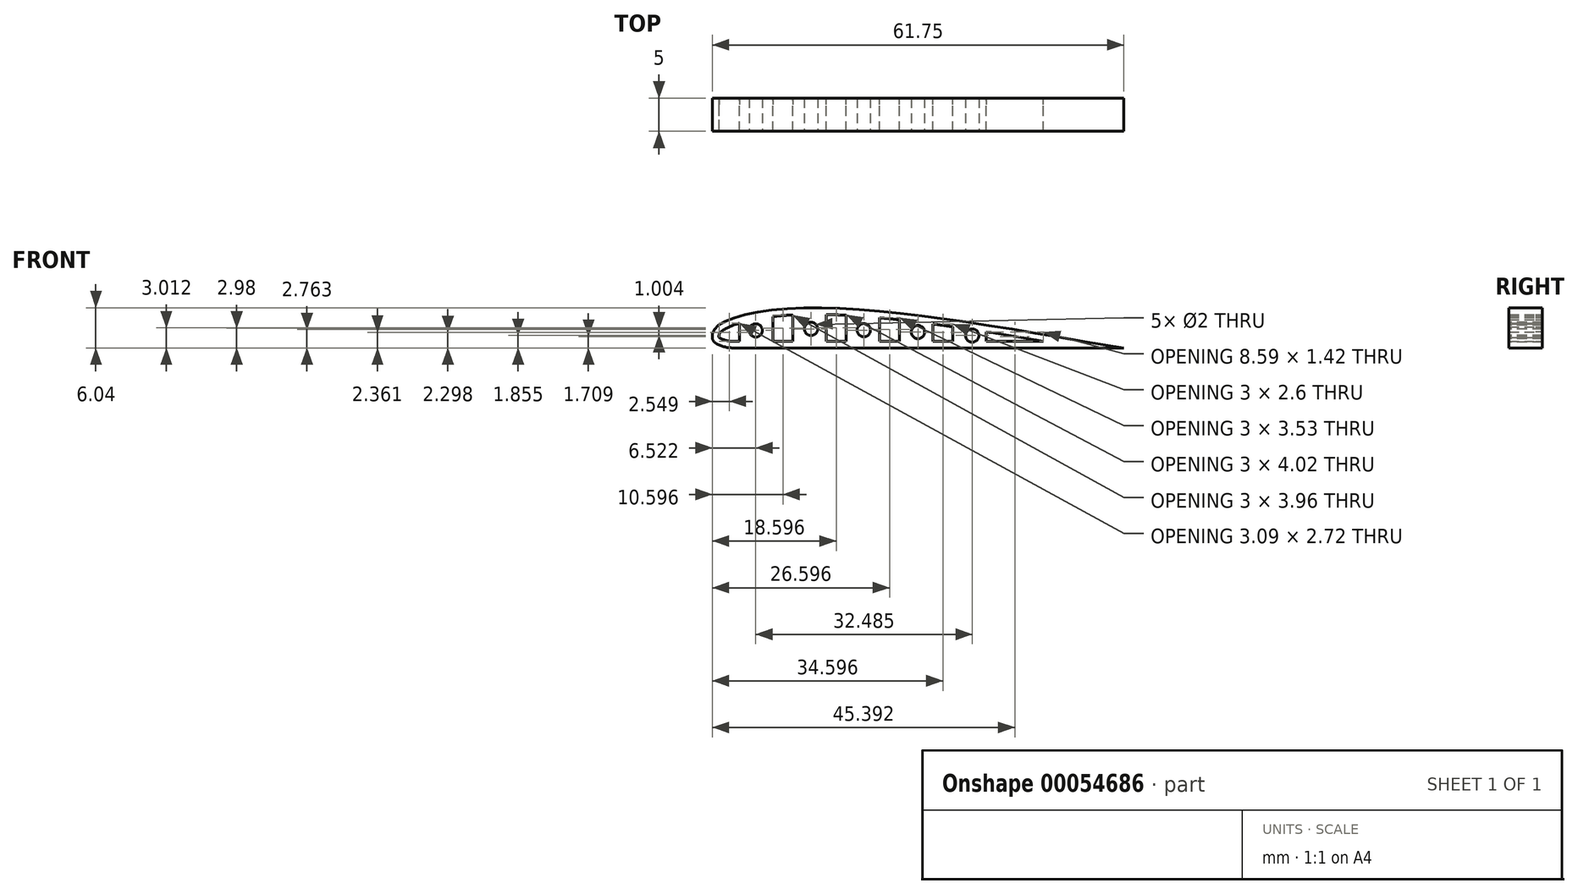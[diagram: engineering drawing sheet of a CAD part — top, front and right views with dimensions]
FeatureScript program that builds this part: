
annotation { "Feature Type Name" : "Feature", "Feature Type Description" : "" }
export const myFeature = defineFeature(function(context is Context, id is Id, definition is map)
    precondition{}
    {
        {
            var Q0;
            Q0=qCreatedBy(makeId("Front.planeOp"),FACE);
            var sketch = newSketch(context, id + "F0", { "sketchPlane" : qUnion([Q0])});
            skLineSegment(sketch, "E0.bottom", {"start": v(-37.5, 15) * mm, "end": v(37.5, 15) * mm});
            skLineSegment(sketch, "E0.top", {"start": v(-37.5, -15) * mm, "end": v(37.5, -15) * mm});
            skLineSegment(sketch, "E0.left", {"start": v(-37.5, 15) * mm, "end": v(-37.5, -15) * mm});
            skLineSegment(sketch, "E0.right", {"start": v(37.5, 15) * mm, "end": v(37.5, -15) * mm});
            skSolve(sketch);
        }
        {
            var Q0;
            Q0=makeQuery(id+"F0.imprint","IMPRINT",FACE,{"disambiguationData":[TD([[makeQuery(id+"F0.imprint","IMPRINT",EDGE,{"derivedFrom":sQuery(id+"F0.wireOp",EDGE,"E0.bottom")}),-1.0]])]});
            var sketch = newSketch(context, id + "F1", { "sketchPlane" : qUnion([Q0])});
            skLineSegment(sketch, "E1", {"start": v(33.64, -15.05) * mm, "end": v(-26.41, -15.05) * mm});
            skLineSegment(sketch, "E2", {"start": v(-26.41, -15.05) * mm, "end": v(33.64, -15.05) * mm});
            skFitSpline(sketch, "E3", {"points": [v(-26.41, -15.05) * mm, v(-27.49, -14.56) * mm, v(-28.34, -13.98) * mm], "startDerivative": vector(-2.16, 0.87) * mm, "endDerivative": vector(-1.68, 1.26) * mm});
            skFitSpline(sketch, "E4", {"points": [v(-28.34, -13.98) * mm, v(-28.07, -12.16) * mm, v(-16.6, -9.05) * mm, v(27.1, -13.98) * mm], "startDerivative": vector(-2.15, 15.6) * mm, "endDerivative": vector(83.94, -14.46) * mm});
            skLineSegment(sketch, "E5", {"start": v(27.1, -13.98) * mm, "end": v(33.64, -15.05) * mm});
            skSolve(sketch);
        }
        {
            var Q0;
            {var subQ0=sQuery(id+"F1.wireOp",EDGE,"E4");Q0=makeQuery(id+"F1.imprint","IMPRINT",FACE,{"disambiguationData":[TD([[makeQuery(id+"F1.imprint","IMPRINT",EDGE,{"derivedFrom":subQ0}),-1.0]])]});}
            extrude(context, id + "F2", {"entities" : qUnion([Q0]), "depth" : 5 * mm});
        }
        {
            var Q0;
            Q0=makeQuery(id+"F2.opExtrude","SWEPT_EDGE",EDGE,{"disambiguationData":[OSD([sQuery(id+"F0.wireOp",EDGE,"E0.top"),sQuery(id+"F1.wireOp",EDGE,"E3")])]});
            fillet(context, id + "F3", {"entities" : qUnion([Q0]), "radius" : 5 * mm, "tangentPropagation" : true, "allowEdgeOverflow" : false});
        }
        {
            var Q0;
            Q0=makeQuery(id+"F2.opExtrude","SWEPT_EDGE",EDGE,{"disambiguationData":[OSD([sQuery(id+"F1.wireOp",EDGE,"E3"),sQuery(id+"F1.wireOp",EDGE,"E4")])]});
            fillet(context, id + "F4", {"entities" : qUnion([Q0]), "radius" : 1 * mm, "tangentPropagation" : true, "allowEdgeOverflow" : false});
        }
        {
            var Q0;
            Q0=makeQuery(id+"F2.opExtrude","CAP_FACE",FACE,{"disambiguationData":[OSD([sQuery(id+"F0.wireOp",EDGE,"E0.top"),sQuery(id+"F1.wireOp",EDGE,"E3"),sQuery(id+"F1.wireOp",EDGE,"E4"),sQuery(id+"F1.wireOp",EDGE,"E5")])],"isStart":false});
            var Q1;
            Q1=makeQuery(id+"F2.opExtrude","SWEPT_BODY",BODY,{"disambiguationData":[OSD([sQuery(id+"F0.wireOp",EDGE,"E0.top"),sQuery(id+"F1.wireOp",EDGE,"E3"),sQuery(id+"F1.wireOp",EDGE,"E4"),sQuery(id+"F1.wireOp",EDGE,"E5")])]});
            shell(context, id + "F5", {"entities" : qUnion([Q0]), "parts" : qUnion([Q1]), "thickness" : 1 * mm});
        }
        {
            var Q0;
            Q0=makeQuery(id+"F5.opShell","OFFSET_FACE",FACE,{"disambiguationData":[OSD([sQuery(id+"F0.wireOp",EDGE,"E0.top"),sQuery(id+"F1.wireOp",EDGE,"E3"),sQuery(id+"F1.wireOp",EDGE,"E4"),sQuery(id+"F1.wireOp",EDGE,"E5")])]});
            extrude(context, id + "F6", {"entities" : qUnion([Q0]), "operationType" : NewBodyOperationType.REMOVE, "oppositeDirection" : true, "depth" : 25 * mm});
        }
        {
            var Q0;
            Q0=qCreatedBy(makeId("Front.planeOp"),FACE);
            var sketch = newSketch(context, id + "F7", { "sketchPlane" : qUnion([Q0])});
            skLineSegment(sketch, "E6", {"start": v(-24.3, -10.76) * mm, "end": v(-24.3, -14.53) * mm});
            skLineSegment(sketch, "E7", {"start": v(-23.3, -10.6) * mm, "end": v(-23.3, -14.66) * mm});
            skLineSegment(sketch, "E8", {"start": v(-20.3, -9.96) * mm, "end": v(-20.3, -14.5) * mm});
            skLineSegment(sketch, "E9", {"start": v(-19.3, -9.97) * mm, "end": v(-19.3, -14.33) * mm});
            skLineSegment(sketch, "E10", {"start": v(-16.3, -9.87) * mm, "end": v(-16.3, -14.17) * mm});
            skLineSegment(sketch, "E11", {"start": v(-15.3, -9.72) * mm, "end": v(-15.3, -14.31) * mm});
            skLineSegment(sketch, "E12", {"start": v(-12.3, -9.67) * mm, "end": v(-12.3, -14.26) * mm});
            skLineSegment(sketch, "E13", {"start": v(-11.3, -9.59) * mm, "end": v(-11.3, -14.23) * mm});
            skLineSegment(sketch, "E14", {"start": v(-8.3, -9.76) * mm, "end": v(-8.3, -14.25) * mm});
            skLineSegment(sketch, "E15", {"start": v(-7.3, -9.69) * mm, "end": v(-7.3, -14.44) * mm});
            skLineSegment(sketch, "E16", {"start": v(-4.3, -9.96) * mm, "end": v(-4.3, -14.17) * mm});
            skLineSegment(sketch, "E17", {"start": v(-3.3, -10.07) * mm, "end": v(-3.3, -14.54) * mm});
            skLineSegment(sketch, "E18", {"start": v(-0.3, -10.3) * mm, "end": v(-0.3, -14.48) * mm});
            skLineSegment(sketch, "E19", {"start": v(0.7, -10.28) * mm, "end": v(0.7, -14.5) * mm});
            skLineSegment(sketch, "E20", {"start": v(3.7, -10.65) * mm, "end": v(3.7, -14.38) * mm});
            skLineSegment(sketch, "E21", {"start": v(4.7, -10.58) * mm, "end": v(4.7, -14.4) * mm});
            skLineSegment(sketch, "E22", {"start": v(7.7, -11.69) * mm, "end": v(7.7, -14.38) * mm});
            skLineSegment(sketch, "E23", {"start": v(8.7, -11.67) * mm, "end": v(8.7, -14.24) * mm});
            skLineSegment(sketch, "E24", {"start": v(11.7, -14.25) * mm, "end": v(11.7, -12.35) * mm});
            skLineSegment(sketch, "E25", {"start": v(12.7, -12.46) * mm, "end": v(12.7, -14.23) * mm});
            skLineSegment(sketch, "E26", {"start": v(-24.3, -10.76) * mm, "end": v(-23.3, -10.6) * mm});
            skLineSegment(sketch, "E27", {"start": v(-24.3, -14.53) * mm, "end": v(-23.3, -14.66) * mm});
            skLineSegment(sketch, "E28", {"start": v(-19.3, -14.33) * mm, "end": v(-20.3, -14.5) * mm});
            skLineSegment(sketch, "E29", {"start": v(-20.31, -10) * mm, "end": v(-19.3, -9.97) * mm});
            skLineSegment(sketch, "E30", {"start": v(-16.3, -9.87) * mm, "end": v(-15.3, -9.72) * mm});
            skLineSegment(sketch, "E31", {"start": v(-16.3, -14.17) * mm, "end": v(-15.3, -14.31) * mm});
            skLineSegment(sketch, "E32", {"start": v(-12.3, -9.67) * mm, "end": v(-11.3, -9.59) * mm});
            skLineSegment(sketch, "E33", {"start": v(-12.16, -14.4) * mm, "end": v(-11.3, -14.23) * mm});
            skLineSegment(sketch, "E34", {"start": v(-12.3, -14.26) * mm, "end": v(-11.3, -14.23) * mm});
            skLineSegment(sketch, "E35", {"start": v(-8.3, -9.76) * mm, "end": v(-7.3, -9.69) * mm});
            skLineSegment(sketch, "E36", {"start": v(-8.3, -14.25) * mm, "end": v(-7.3, -14.44) * mm});
            skLineSegment(sketch, "E37", {"start": v(-4.3, -14.17) * mm, "end": v(-3.3, -14.54) * mm});
            skLineSegment(sketch, "E38", {"start": v(-4.3, -9.96) * mm, "end": v(-3.3, -10.07) * mm});
            skLineSegment(sketch, "E39", {"start": v(-0.3, -10.3) * mm, "end": v(0.7, -10.28) * mm});
            skLineSegment(sketch, "E40", {"start": v(3.7, -10.65) * mm, "end": v(4.7, -10.58) * mm});
            skLineSegment(sketch, "E41", {"start": v(-0.3, -14.48) * mm, "end": v(0.7, -14.5) * mm});
            skLineSegment(sketch, "E42", {"start": v(3.7, -14.38) * mm, "end": v(4.7, -14.4) * mm});
            skLineSegment(sketch, "E43", {"start": v(8.7, -14.24) * mm, "end": v(7.7, -14.38) * mm});
            skLineSegment(sketch, "E44", {"start": v(11.7, -14.25) * mm, "end": v(12.7, -14.23) * mm});
            skLineSegment(sketch, "E45", {"start": v(12.7, -12.46) * mm, "end": v(11.7, -12.35) * mm});
            skLineSegment(sketch, "E46", {"start": v(8.7, -11.67) * mm, "end": v(7.7, -11.69) * mm});
            skLineSegment(sketch, "E47", {"start": v(-23.3, -10.6) * mm, "end": v(-20.3, -9.96) * mm});
            skLineSegment(sketch, "E48", {"start": v(-20.3, -14.5) * mm, "end": v(-23.3, -14.66) * mm});
            skLineSegment(sketch, "E49", {"start": v(-15.3, -9.72) * mm, "end": v(-12.3, -9.67) * mm});
            skLineSegment(sketch, "E50", {"start": v(-15.3, -14.31) * mm, "end": v(-12.3, -14.26) * mm});
            skLineSegment(sketch, "E51", {"start": v(-7.3, -14.44) * mm, "end": v(-4.3, -14.17) * mm});
            skLineSegment(sketch, "E52", {"start": v(-7.3, -9.69) * mm, "end": v(-4.3, -9.96) * mm});
            skLineSegment(sketch, "E53", {"start": v(0.7, -10.28) * mm, "end": v(3.7, -10.65) * mm});
            skLineSegment(sketch, "E54", {"start": v(0.7, -14.5) * mm, "end": v(3.7, -14.38) * mm});
            skLineSegment(sketch, "E55", {"start": v(8.7, -11.67) * mm, "end": v(11.7, -12.35) * mm});
            skLineSegment(sketch, "E56", {"start": v(8.7, -14.24) * mm, "end": v(11.7, -14.25) * mm});
            skSolve(sketch);
        }
        {
            var Q0;
            Q0=makeQuery(id+"F7.imprint","IMPRINT",FACE,{"disambiguationData":[TD([[makeQuery(id+"F7.imprint","IMPRINT",EDGE,{"derivedFrom":sQuery(id+"F7.wireOp",EDGE,"E22")}),1.0]])]});
            var Q1;
            Q1=makeQuery(id+"F7.imprint","IMPRINT",FACE,{"disambiguationData":[TD([[makeQuery(id+"F7.imprint","IMPRINT",EDGE,{"derivedFrom":sQuery(id+"F7.wireOp",EDGE,"E6")}),1.0]])]});
            var Q2;
            {var subQ4=sQuery(id+"F7.wireOp",EDGE,"E9");Q2=makeQuery(id+"F7.imprint","IMPRINT",FACE,{"disambiguationData":[TD([[makeQuery(id+"F7.imprint","IMPRINT",EDGE,{"derivedFrom":subQ4}),-1.0]])]});}
            var Q3;
            Q3=makeQuery(id+"F7.imprint","IMPRINT",FACE,{"disambiguationData":[TD([[makeQuery(id+"F7.imprint","IMPRINT",EDGE,{"derivedFrom":sQuery(id+"F7.wireOp",EDGE,"E10")}),1.0]])]});
            var Q4;
            Q4=makeQuery(id+"F7.imprint","IMPRINT",FACE,{"disambiguationData":[TD([[makeQuery(id+"F7.imprint","IMPRINT",EDGE,{"derivedFrom":sQuery(id+"F7.wireOp",EDGE,"E12")}),1.0]])]});
            var Q5;
            Q5=makeQuery(id+"F7.imprint","IMPRINT",FACE,{"disambiguationData":[TD([[makeQuery(id+"F7.imprint","IMPRINT",EDGE,{"derivedFrom":sQuery(id+"F7.wireOp",EDGE,"E14")}),1.0]])]});
            var Q6;
            Q6=makeQuery(id+"F7.imprint","IMPRINT",FACE,{"disambiguationData":[TD([[makeQuery(id+"F7.imprint","IMPRINT",EDGE,{"derivedFrom":sQuery(id+"F7.wireOp",EDGE,"E16")}),1.0]])]});
            var Q7;
            Q7=makeQuery(id+"F7.imprint","IMPRINT",FACE,{"disambiguationData":[TD([[makeQuery(id+"F7.imprint","IMPRINT",EDGE,{"derivedFrom":sQuery(id+"F7.wireOp",EDGE,"E18")}),1.0]])]});
            var Q8;
            Q8=makeQuery(id+"F7.imprint","IMPRINT",FACE,{"disambiguationData":[TD([[makeQuery(id+"F7.imprint","IMPRINT",EDGE,{"derivedFrom":sQuery(id+"F7.wireOp",EDGE,"E20")}),1.0]])]});
            var Q9;
            Q9=makeQuery(id+"F7.imprint","IMPRINT",FACE,{"disambiguationData":[TD([[makeQuery(id+"F7.imprint","IMPRINT",EDGE,{"derivedFrom":sQuery(id+"F7.wireOp",EDGE,"E24")}),-1.0]])]});
            extrude(context, id + "F8", {"entities" : qUnion([Q0, Q1, Q2, Q3, Q4, Q5, Q6, Q7, Q8, Q9]), "operationType" : NewBodyOperationType.ADD, "depth" : 5 * mm});
        }
        {
            var Q0;
            Q0=makeQuery(id+"F7.imprint","IMPRINT",FACE,{"disambiguationData":[TD([[makeQuery(id+"F7.imprint","IMPRINT",EDGE,{"derivedFrom":sQuery(id+"F7.wireOp",EDGE,"E11")}),1.0]])]});
            var Q1;
            Q1=makeQuery(id+"F7.imprint","IMPRINT",FACE,{"disambiguationData":[TD([[makeQuery(id+"F7.imprint","IMPRINT",EDGE,{"derivedFrom":sQuery(id+"F7.wireOp",EDGE,"E15")}),1.0]])]});
            var Q2;
            Q2=makeQuery(id+"F7.imprint","IMPRINT",FACE,{"disambiguationData":[TD([[makeQuery(id+"F7.imprint","IMPRINT",EDGE,{"derivedFrom":sQuery(id+"F7.wireOp",EDGE,"E23")}),1.0]])]});
            var Q3;
            Q3=makeQuery(id+"F7.imprint","IMPRINT",FACE,{"disambiguationData":[TD([[makeQuery(id+"F7.imprint","IMPRINT",EDGE,{"derivedFrom":sQuery(id+"F7.wireOp",EDGE,"E7")}),1.0]])]});
            var Q4;
            Q4=makeQuery(id+"F7.imprint","IMPRINT",FACE,{"disambiguationData":[TD([[makeQuery(id+"F7.imprint","IMPRINT",EDGE,{"derivedFrom":sQuery(id+"F7.wireOp",EDGE,"E19")}),1.0]])]});
            extrude(context, id + "F9", {"entities" : qUnion([Q0, Q1, Q2, Q3, Q4]), "operationType" : NewBodyOperationType.ADD, "depth" : 5 * mm});
        }
        {
            var Q0;
            {var subQ0=sQuery(id+"F7.wireOp",EDGE,"E24");var subQ1=sQuery(id+"F7.wireOp",EDGE,"E23");var subQ2=sQuery(id+"F7.wireOp",EDGE,"E20");var subQ3=sQuery(id+"F7.wireOp",EDGE,"E19");var subQ4=sQuery(id+"F7.wireOp",EDGE,"E16");var subQ5=sQuery(id+"F7.wireOp",EDGE,"E15");var subQ6=sQuery(id+"F7.wireOp",EDGE,"E12");var subQ7=sQuery(id+"F7.wireOp",EDGE,"E11");var subQ8=sQuery(id+"F7.wireOp",EDGE,"E8");var subQ9=sQuery(id+"F7.wireOp",EDGE,"E7");Q0=makeQuery(id+"F9.boolean.opBoolean","MERGE",FACE,{"derivedFrom":[makeQuery(id+"F8.boolean.opBoolean","MERGE",FACE,{"derivedFrom":[makeQuery(id+"F2.opExtrude","CAP_FACE",FACE,{"disambiguationData":[OSD([sQuery(id+"F0.wireOp",EDGE,"E0.top"),sQuery(id+"F1.wireOp",EDGE,"E3"),sQuery(id+"F1.wireOp",EDGE,"E4"),sQuery(id+"F1.wireOp",EDGE,"E5")])],"isStart":false}),makeQuery(id+"F8.opExtrude","CAP_FACE",FACE,{"disambiguationData":[OSD([sQuery(id+"F7.wireOp",EDGE,"E6"),subQ9,sQuery(id+"F7.wireOp",EDGE,"E26"),sQuery(id+"F7.wireOp",EDGE,"E27")])],"isStart":false}),makeQuery(id+"F8.opExtrude","CAP_FACE",FACE,{"disambiguationData":[OSD([subQ8,sQuery(id+"F7.wireOp",EDGE,"E9"),sQuery(id+"F7.wireOp",EDGE,"E28"),sQuery(id+"F7.wireOp",EDGE,"E29")])],"isStart":false}),makeQuery(id+"F8.opExtrude","CAP_FACE",FACE,{"disambiguationData":[OSD([sQuery(id+"F7.wireOp",EDGE,"E10"),subQ7,sQuery(id+"F7.wireOp",EDGE,"E30"),sQuery(id+"F7.wireOp",EDGE,"E31")])],"isStart":false}),makeQuery(id+"F8.opExtrude","CAP_FACE",FACE,{"disambiguationData":[OSD([subQ6,sQuery(id+"F7.wireOp",EDGE,"E13"),sQuery(id+"F7.wireOp",EDGE,"E32"),sQuery(id+"F7.wireOp",EDGE,"E34")])],"isStart":false}),makeQuery(id+"F8.opExtrude","CAP_FACE",FACE,{"disambiguationData":[OSD([sQuery(id+"F7.wireOp",EDGE,"E14"),subQ5,sQuery(id+"F7.wireOp",EDGE,"E35"),sQuery(id+"F7.wireOp",EDGE,"E36")])],"isStart":false}),makeQuery(id+"F8.opExtrude","CAP_FACE",FACE,{"disambiguationData":[OSD([subQ4,sQuery(id+"F7.wireOp",EDGE,"E17"),sQuery(id+"F7.wireOp",EDGE,"E37"),sQuery(id+"F7.wireOp",EDGE,"E38")])],"isStart":false}),makeQuery(id+"F8.opExtrude","CAP_FACE",FACE,{"disambiguationData":[OSD([sQuery(id+"F7.wireOp",EDGE,"E18"),subQ3,sQuery(id+"F7.wireOp",EDGE,"E39"),sQuery(id+"F7.wireOp",EDGE,"E41")])],"isStart":false}),makeQuery(id+"F8.opExtrude","CAP_FACE",FACE,{"disambiguationData":[OSD([subQ2,sQuery(id+"F7.wireOp",EDGE,"E21"),sQuery(id+"F7.wireOp",EDGE,"E40"),sQuery(id+"F7.wireOp",EDGE,"E42")])],"isStart":false}),makeQuery(id+"F8.opExtrude","CAP_FACE",FACE,{"disambiguationData":[OSD([sQuery(id+"F7.wireOp",EDGE,"E22"),subQ1,sQuery(id+"F7.wireOp",EDGE,"E43"),sQuery(id+"F7.wireOp",EDGE,"E46")])],"isStart":false}),makeQuery(id+"F8.opExtrude","CAP_FACE",FACE,{"disambiguationData":[OSD([subQ0,sQuery(id+"F7.wireOp",EDGE,"E25"),sQuery(id+"F7.wireOp",EDGE,"E44"),sQuery(id+"F7.wireOp",EDGE,"E45")])],"isStart":false})]}),makeQuery(id+"F9.opExtrude","CAP_FACE",FACE,{"disambiguationData":[OSD([subQ9,subQ8,sQuery(id+"F7.wireOp",EDGE,"E47"),sQuery(id+"F7.wireOp",EDGE,"E48")])],"isStart":false}),makeQuery(id+"F9.opExtrude","CAP_FACE",FACE,{"disambiguationData":[OSD([subQ7,subQ6,sQuery(id+"F7.wireOp",EDGE,"E49"),sQuery(id+"F7.wireOp",EDGE,"E50")])],"isStart":false}),makeQuery(id+"F9.opExtrude","CAP_FACE",FACE,{"disambiguationData":[OSD([subQ5,subQ4,sQuery(id+"F7.wireOp",EDGE,"E51"),sQuery(id+"F7.wireOp",EDGE,"E52")])],"isStart":false}),makeQuery(id+"F9.opExtrude","CAP_FACE",FACE,{"disambiguationData":[OSD([subQ3,subQ2,sQuery(id+"F7.wireOp",EDGE,"E53"),sQuery(id+"F7.wireOp",EDGE,"E54")])],"isStart":false}),makeQuery(id+"F9.opExtrude","CAP_FACE",FACE,{"disambiguationData":[OSD([subQ1,subQ0,sQuery(id+"F7.wireOp",EDGE,"E55"),sQuery(id+"F7.wireOp",EDGE,"E56")])],"isStart":false})]});}
            var sketch = newSketch(context, id + "F10", { "sketchPlane" : qUnion([Q0])});
            skCircle(sketch, "E57", {"center": v(-21.88, -12.37) * mm, "radius": 1 * mm});
            skCircle(sketch, "E58", {"center": v(-13.58, -12.14) * mm, "radius": 1 * mm});
            skCircle(sketch, "E59", {"center": v(-5.67, -12.33) * mm, "radius": 1 * mm});
            skCircle(sketch, "E60", {"center": v(10.6, -13.15) * mm, "radius": 1 * mm});
            skCircle(sketch, "E61", {"center": v(2.46, -12.61) * mm, "radius": 1 * mm});
            skSolve(sketch);
        }
        {
            var Q0;
            Q0=makeQuery(id+"F10.imprint","IMPRINT",FACE,{"disambiguationData":[TD([[makeQuery(id+"F10.imprint","IMPRINT",EDGE,{"derivedFrom":sQuery(id+"F10.wireOp",EDGE,"E57")}),1.0]])]});
            var Q1;
            Q1=makeQuery(id+"F10.imprint","IMPRINT",FACE,{"disambiguationData":[TD([[makeQuery(id+"F10.imprint","IMPRINT",EDGE,{"derivedFrom":sQuery(id+"F10.wireOp",EDGE,"E58")}),1.0]])]});
            var Q2;
            Q2=makeQuery(id+"F10.imprint","IMPRINT",FACE,{"disambiguationData":[TD([[makeQuery(id+"F10.imprint","IMPRINT",EDGE,{"derivedFrom":sQuery(id+"F10.wireOp",EDGE,"E59")}),1.0]])]});
            var Q3;
            Q3=makeQuery(id+"F10.imprint","IMPRINT",FACE,{"disambiguationData":[TD([[makeQuery(id+"F10.imprint","IMPRINT",EDGE,{"derivedFrom":sQuery(id+"F10.wireOp",EDGE,"E61")}),1.0]])]});
            var Q4;
            Q4=makeQuery(id+"F10.imprint","IMPRINT",FACE,{"disambiguationData":[TD([[makeQuery(id+"F10.imprint","IMPRINT",EDGE,{"derivedFrom":sQuery(id+"F10.wireOp",EDGE,"E60")}),1.0]])]});
            extrude(context, id + "F11", {"entities" : qUnion([Q0, Q1, Q2, Q3, Q4]), "operationType" : NewBodyOperationType.REMOVE, "oppositeDirection" : true, "depth" : 25 * mm});
        }
    });
